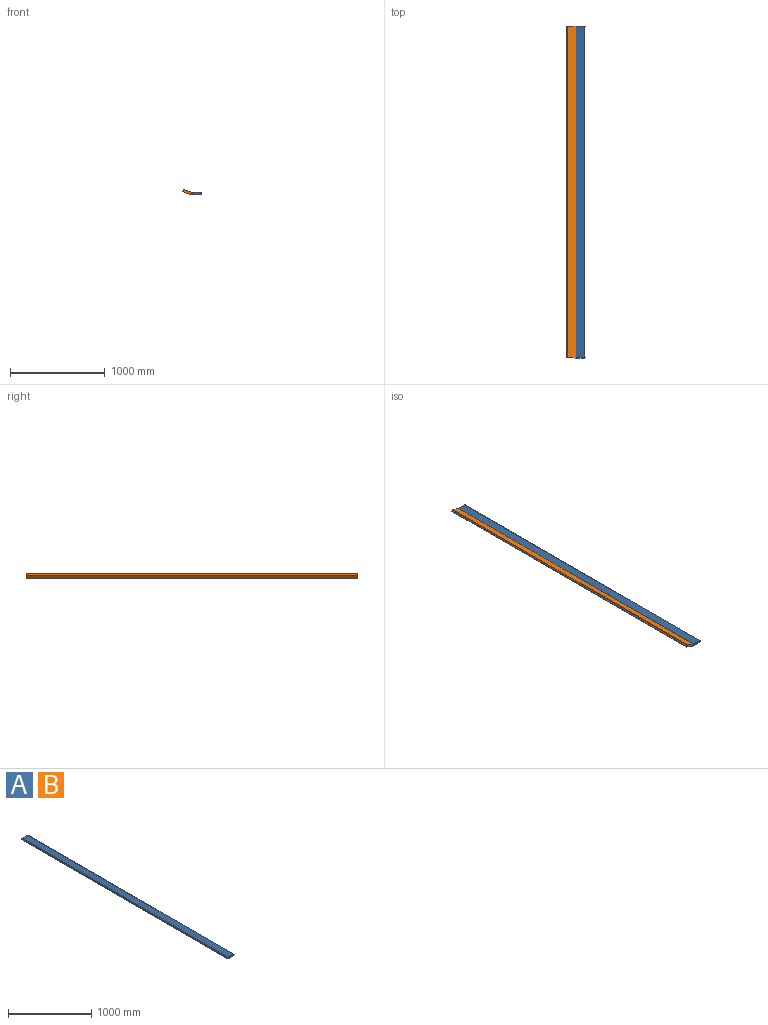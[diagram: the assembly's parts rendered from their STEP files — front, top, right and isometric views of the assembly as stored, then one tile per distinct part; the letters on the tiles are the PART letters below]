
ASSEMBLY  parts=2 mates=1
PART A: 14 faces, bbox 105x3500x25 mm
  f0: plane 3500x91mm, normal (0,0,1), area 318500mm2, adj f8,f9,f11,f13
  f1: plane 3500x1.84mm, normal (-1,0,0), area 6439.1mm2, adj f2,f8,f9,f13
  f2: cylinder r=10mm len=3500mm, axis (0,1,0), area 73303.8mm2, adj f1,f3,f8,f9
  f3: plane 3500x1.84mm, normal (-1,0,0), area 6439.1mm2, adj f2,f8,f9,f12
  f4: plane 3500x91mm, normal (0,0,-1), area 318500mm2, adj f8,f9,f10,f12
  f5: plane 3500x0.5mm, normal (1,0,0), area 1750mm2, adj f6,f8,f9,f10
  f6: cylinder r=10mm len=3500mm, axis (0,1,0), area 109955.7mm2, adj f5,f7,f8,f9
  f7: plane 3500x0.5mm, normal (1,0,0), area 1750mm2, adj f6,f8,f9,f11
  f8: plane 105x25mm, normal (0,-1,0), area 2462.7mm2, adj f0,f1,f2,f3,f4,f5,f6,f7
  f9: plane 105x25mm, normal (0,1,0), area 2462.7mm2, adj f0,f1,f2,f3,f4,f5,f6,f7
  f10: plane 3500x2mm, normal (0.71,0,-0.71), area 9899.5mm2, adj f4,f5,f8,f9
  f11: plane 3500x2mm, normal (0.71,0,0.71), area 9899.5mm2, adj f0,f7,f8,f9
  f12: plane 3500x2mm, normal (-0.71,0,-0.71), area 9899.5mm2, adj f3,f4,f8,f9
  f13: plane 3500x2mm, normal (-0.71,0,0.71), area 9899.5mm2, adj f0,f1,f8,f9
PART B: same geometry as A
PLACE A at identity fixed
PLACE B rot(axis=(0,1,0),19.6deg) t=(-93.22,0,16.09)mm
MATE planar B.f8 <-> A.f8  axis (0,-1,0) through (-89.05,-3500,14.6)mm
